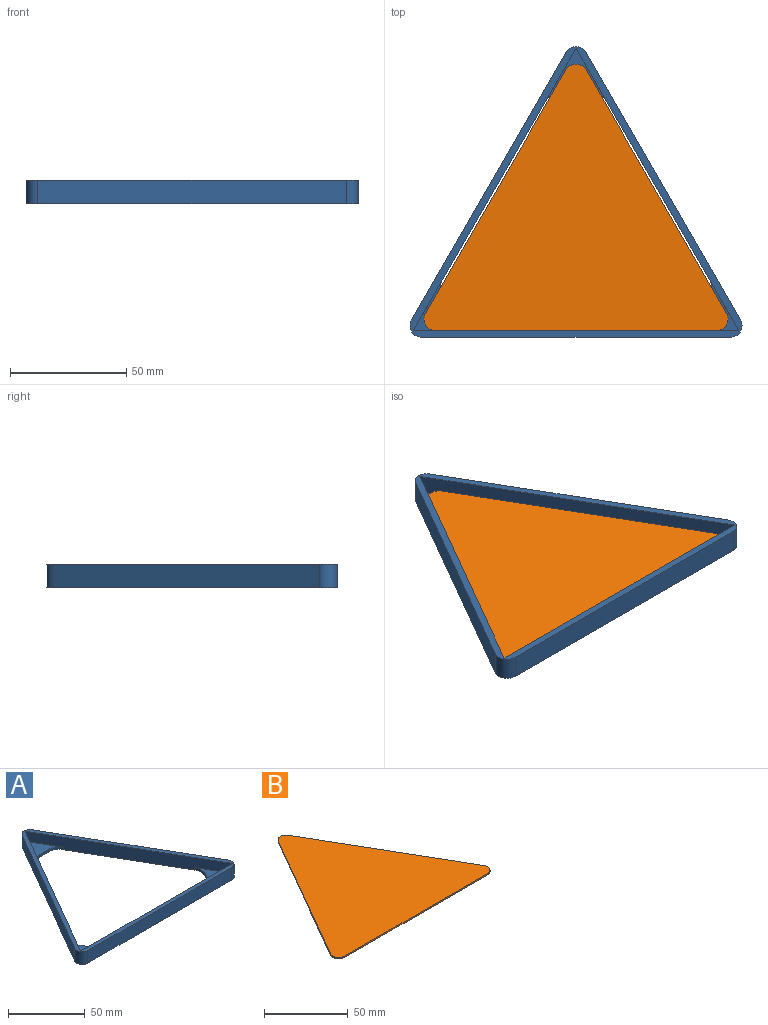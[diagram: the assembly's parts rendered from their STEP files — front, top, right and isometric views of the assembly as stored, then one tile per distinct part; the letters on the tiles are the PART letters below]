
ASSEMBLY  parts=2 mates=1
PART A: 23 faces, bbox 142.7x124.9x10 mm
  f0: plane 140x10mm, normal (0,1,0), area 1296.9mm2, adj f1,f4,f6,f7,f11,f13,f14,f17
  f1: plane 121.24x70mm, normal (0.87,-0.5,0), area 1296.9mm2, adj f0,f4,f6,f7,f9,f11,f16,f18
  f2: plane 132.68x10mm, normal (0,-1,0), area 1326.8mm2, adj f6,f7,f20,f22
  f3: plane 114.9x66.34mm, normal (0.87,0.5,0), area 1326.8mm2, adj f6,f7,f20,f21
  f4: plane 121.24x70mm, normal (-0.87,-0.5,0), area 1296.9mm2, adj f0,f1,f6,f7,f9,f13,f15,f19
  f5: plane 114.9x66.34mm, normal (-0.87,0.5,0), area 1326.8mm2, adj f6,f7,f21,f22
  f6: plane 142.68x124.9mm, normal (0,0,1), area 1204.4mm2, adj f0,f1,f2,f3,f4,f5,f20,f21
  f7: plane 142.68x124.9mm, normal (0,0,-1), area 1756.2mm2, adj f0,f1,f2,f3,f4,f5,f8,f10
  f8: plane 8.45x2mm, normal (0,-1,0), area 16.9mm2, adj f7,f9,f18,f19
  f9: plane 25.77x22.32mm, normal (0,0,1), area 184mm2, adj f1,f4,f8,f18,f19
  f10: plane 7.32x4.23mm, normal (0.87,0.5,0), area 16.9mm2, adj f7,f11,f16,f17
  f11: plane 25.77x22.32mm, normal (0,0,1), area 184mm2, adj f0,f1,f10,f16,f17
  f12: plane 7.32x4.23mm, normal (-0.87,0.5,0), area 16.9mm2, adj f7,f13,f14,f15
  f13: plane 25.77x22.32mm, normal (0,0,1), area 184mm2, adj f0,f4,f12,f14,f15
  f14: cylinder r=10mm len=8.66mm, axis (0,0,1), area 20.9mm2, adj f0,f7,f12,f13
  f15: cylinder r=10mm len=10mm, axis (0,0,1), area 20.9mm2, adj f4,f7,f12,f13
  f16: cylinder r=10mm len=10mm, axis (0,0,1), area 20.9mm2, adj f1,f7,f10,f11
  f17: cylinder r=10mm len=8.66mm, axis (0,0,1), area 20.9mm2, adj f0,f7,f10,f11
  f18: cylinder r=10mm len=8.66mm, axis (0,0,-1), area 20.9mm2, adj f1,f7,f8,f9
  f19: cylinder r=10mm len=8.66mm, axis (0,0,-1), area 20.9mm2, adj f4,f7,f8,f9
  f20: cylinder r=5mm len=10mm, axis (0,0,-1), area 104.7mm2, adj f2,f3,f6,f7
  f21: cylinder r=5mm len=10mm, axis (0,0,-1), area 104.7mm2, adj f3,f5,f6,f7
  f22: cylinder r=5mm len=10mm, axis (0,0,-1), area 104.7mm2, adj f2,f5,f6,f7
PART B: 8 faces, bbox 130.7x114.5x1 mm
  f0: plane 120.68x1mm, normal (0,-1,0), area 120.7mm2, adj f3,f4,f5,f7
  f1: plane 104.51x60.34mm, normal (0.87,0.5,0), area 120.7mm2, adj f3,f4,f5,f6
  f2: plane 104.51x60.34mm, normal (-0.87,0.5,0), area 120.7mm2, adj f3,f4,f6,f7
  f3: plane 130.68x114.51mm, normal (0,0,1), area 8194.9mm2, adj f0,f1,f2,f5,f6,f7
  f4: plane 130.68x114.51mm, normal (0,0,-1), area 8194.9mm2, adj f0,f1,f2,f5,f6,f7
  f5: cylinder r=5mm len=7.5mm, axis (0,0,-1), area 10.5mm2, adj f0,f1,f3,f4
  f6: cylinder r=5mm len=8.66mm, axis (0,0,-1), area 10.5mm2, adj f1,f2,f3,f4
  f7: cylinder r=5mm len=7.5mm, axis (0,0,-1), area 10.5mm2, adj f0,f2,f3,f4
PLACE A t=(-34.37,9,-5)mm fixed
PLACE B t=(-34.37,8.42,-1.3)mm
MATE slider B.f3 <-> A.f6  axis (0,0,1) through (-34.37,-31.41,-0.3)mm
